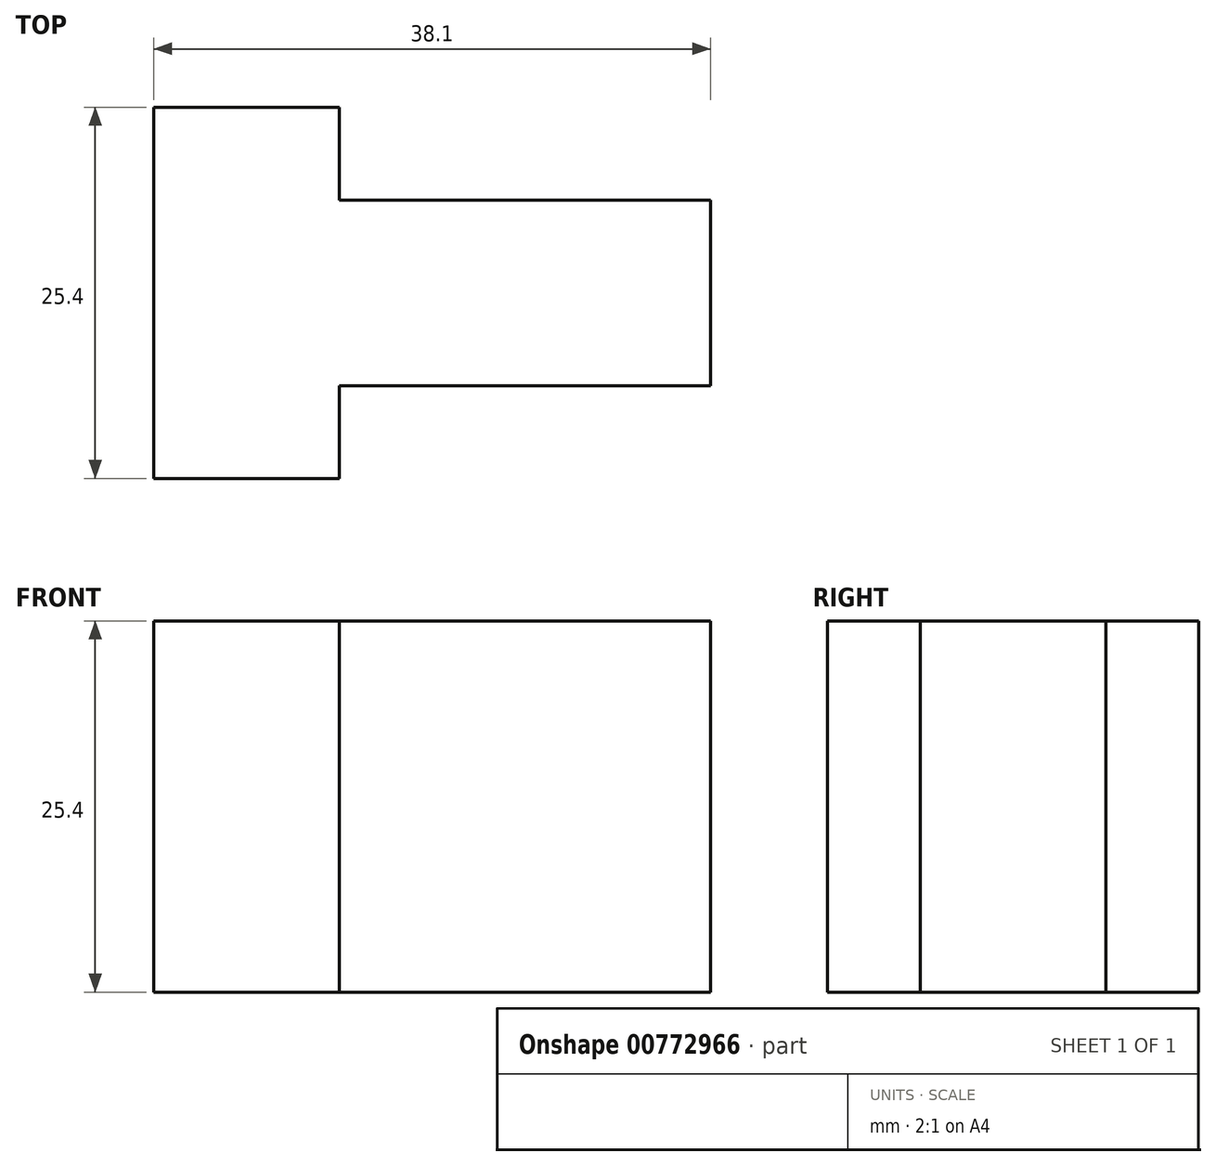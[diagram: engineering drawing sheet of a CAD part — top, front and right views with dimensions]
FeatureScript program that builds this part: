
annotation { "Feature Type Name" : "Feature", "Feature Type Description" : "" }
export const myFeature = defineFeature(function(context is Context, id is Id, definition is map)
    precondition{}
    {
        {
            var Q0;
            Q0=qCreatedBy(makeId("Top.planeOp"),FACE);
            var sketch = newSketch(context, id + "F0", { "sketchPlane" : qUnion([Q0])});
            skLineSegment(sketch, "E0", {"start": v(0, 0) * mm, "end": v(25.4, 0) * mm});
            skLineSegment(sketch, "E1", {"start": v(25.4, 0) * mm, "end": v(25.4, 12.7) * mm});
            skLineSegment(sketch, "E2", {"start": v(25.4, 12.7) * mm, "end": v(0, 12.7) * mm});
            skLineSegment(sketch, "E3", {"start": v(0, 12.7) * mm, "end": v(0, 19.05) * mm});
            skLineSegment(sketch, "E4", {"start": v(0, 19.05) * mm, "end": v(-12.7, 19.05) * mm});
            skLineSegment(sketch, "E5", {"start": v(0, 0) * mm, "end": v(0, -6.35) * mm});
            skLineSegment(sketch, "E6", {"start": v(0, -6.35) * mm, "end": v(-12.7, -6.35) * mm});
            skLineSegment(sketch, "E7", {"start": v(-12.7, 19.05) * mm, "end": v(-12.7, -6.35) * mm});
            skSolve(sketch);
        }
        {
            var Q0;
            Q0 = qSketchRegion(id + "F0", true);
            extrude(context, id + "F1", {"entities" : qUnion([Q0]), "depth" : 25.4 * mm, "offsetDistance" : 25.4 * mm});
        }
    });
